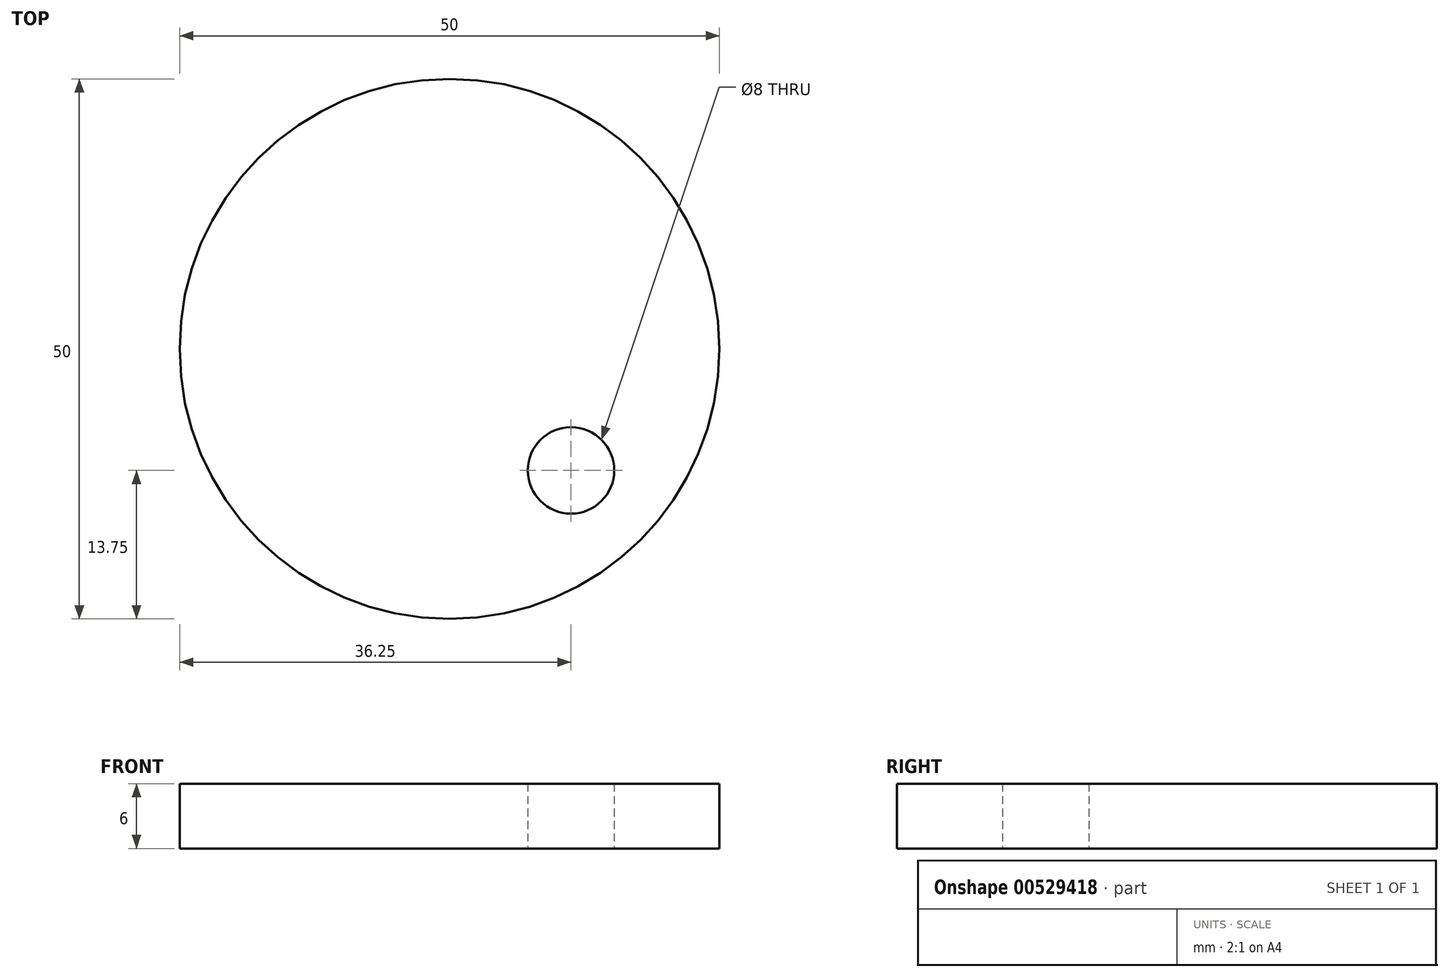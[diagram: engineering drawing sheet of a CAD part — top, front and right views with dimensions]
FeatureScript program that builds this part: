
annotation { "Feature Type Name" : "Feature", "Feature Type Description" : "" }
export const myFeature = defineFeature(function(context is Context, id is Id, definition is map)
    precondition{}
    {
        {
            var Q0;
            Q0=qCreatedBy(makeId("Top.planeOp"),FACE);
            var sketch = newSketch(context, id + "F0", { "sketchPlane" : qUnion([Q0])});
            skCircle(sketch, "E0", {"center": v(0, 0) * mm, "radius": 25 * mm});
            skCircle(sketch, "E1", {"center": v(11.25, -11.25) * mm, "radius": 4 * mm});
            skLineSegment(sketch, "E2", {"start": v(0, -25) * mm, "end": v(0, -11.25) * mm});
            skLineSegment(sketch, "E3", {"start": v(-25, 0) * mm, "end": v(11.25, 0) * mm, "construction": true});
            skLineSegment(sketch, "E4", {"start": v(11.25, -11.25) * mm, "end": v(0, -11.25) * mm});
            skLineSegment(sketch, "E5", {"start": v(11.25, -11.25) * mm, "end": v(11.25, 0) * mm});
            skLineSegment(sketch, "E6", {"start": v(11.25, 0) * mm, "end": v(25, 0) * mm});
            skLineSegment(sketch, "E7", {"start": v(0, -11.25) * mm, "end": v(0, 25) * mm, "construction": true});
            skSolve(sketch);
        }
        {
            var Q0;
            {var subQ1=sQuery(id+"F0.wireOp",EDGE,"E2");Q0=makeQuery(id+"F0.imprint","IMPRINT",FACE,{"disambiguationData":[TD([[makeQuery(id+"F0.imprint","IMPRINT",EDGE,{"derivedFrom":subQ1}),1.0]])]});}
            var Q1;
            {var subQ0=sQuery(id+"F0.wireOp",EDGE,"E2");Q1=makeQuery(id+"F0.imprint","IMPRINT",FACE,{"disambiguationData":[TD([[makeQuery(id+"F0.imprint","IMPRINT",EDGE,{"derivedFrom":subQ0}),-1.0]])]});}
            extrude(context, id + "F1", {"entities" : qUnion([Q0, Q1]), "depth" : 6 * mm, "offsetDistance" : 25 * mm});
        }
    });
